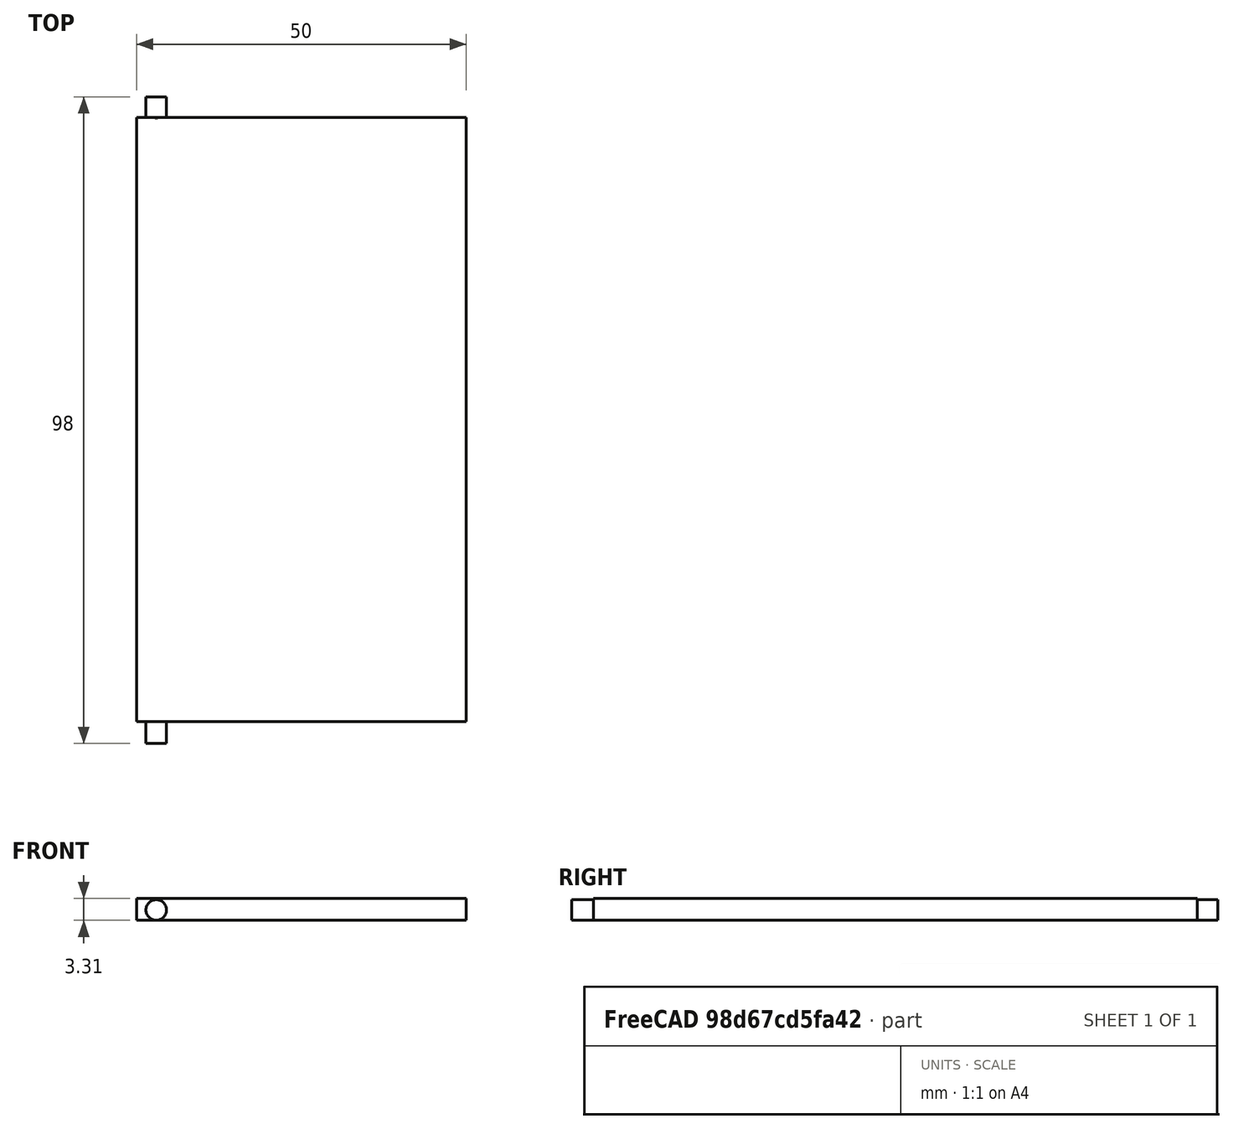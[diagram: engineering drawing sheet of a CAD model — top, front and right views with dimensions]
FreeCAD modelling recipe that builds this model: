
FCSTD DOCUMENT  (FreeCAD 0.20R29603 (Git))
Label: shuffle-flap
License: All rights reserved
LicenseURL: http://en.wikipedia.org/wiki/All_rights_reserved
objects: PartDesign::AdditiveCylinder×2, PartDesign::AdditiveBox×1, PartDesign::Body×1
note: 7 computed .brp shape members not serialized (recipe doc carries the construction recipe); baked Part::Feature solids carry a one-line shape summary decoded from their .brp

FEATURE [PartDesign::AdditiveBox] Box
  AttacherType = Attacher::AttachEngine3D
  Height = 3.3
  Length = 50
  Width = 91.6
FEATURE [PartDesign::AdditiveCylinder] Cylinder
  Angle = 360
  AttacherType = Attacher::AttachEngine3D
  AttachmentOffset = pos=(3,1.55,0) rot=(0,0,1;0rad)
  BaseFeature = -> Box
  FirstAngle = 0
  Height = 3.3
  MapMode = 5
  Placement = pos=(3,3e-16,1.55) rot=(1,0,0;1.5708rad)
  Radius = 1.56
  SecondAngle = 0
  Support = -> [Box]
FEATURE [PartDesign::AdditiveCylinder] Cylinder001
  Angle = 360
  AttacherType = Attacher::AttachEngine3D
  AttachmentOffset = pos=(0,0,-98) rot=(0,0,1;0rad)
  BaseFeature = -> Cylinder
  FirstAngle = 0
  Height = 3.3
  MapMode = 5
  Placement = pos=(3,94.7,1.55) rot=(1,0,0;1.5708rad)
  Radius = 1.56
  SecondAngle = 0
  Support = -> [Cylinder]
FEATURE [PartDesign::Body] Body
  Group = -> [Box,Cylinder,Cylinder001]
  Origin = -> Origin
  Tip = -> Cylinder001
